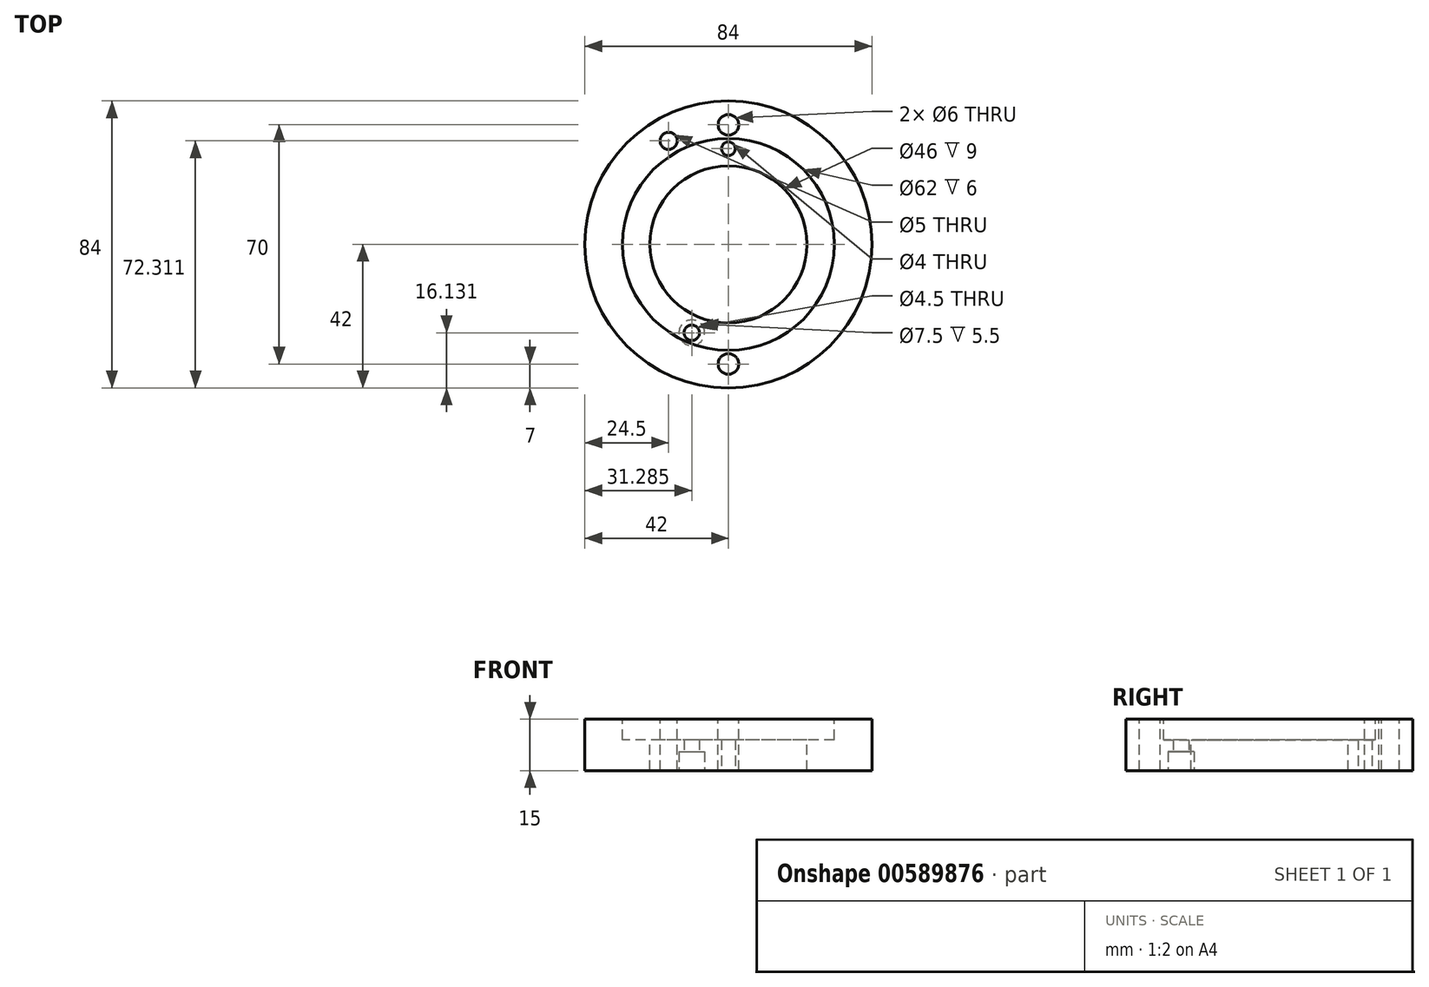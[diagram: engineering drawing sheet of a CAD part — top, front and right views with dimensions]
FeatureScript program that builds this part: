
annotation { "Feature Type Name" : "Feature", "Feature Type Description" : "" }
export const myFeature = defineFeature(function(context is Context, id is Id, definition is map)
    precondition{}
    {
        {
            var Q0;
            Q0=qCreatedBy(makeId("Top.planeOp"),FACE);
            var sketch = newSketch(context, id + "F0", { "sketchPlane" : qUnion([Q0])});
            skCircle(sketch, "E0", {"center": v(0, 0) * mm, "radius": 42 * mm});
            skCircle(sketch, "E1", {"center": v(0, 0) * mm, "radius": 23 * mm});
            skSolve(sketch);
        }
        {
            var Q0;
            Q0 = qSketchRegion(id + "F0", true);
            extrude(context, id + "F1", {"entities" : qUnion([Q0]), "oppositeDirection" : true, "depth" : 15 * mm, "offsetDistance" : 25 * mm});
        }
        {
            var Q0;
            Q0=makeQuery(id+"F1.opExtrude","CAP_FACE",FACE,{"disambiguationData":[OSD([sQuery(id+"F0.wireOp",EDGE,"E0"),sQuery(id+"F0.wireOp",EDGE,"E1")])],"isStart":true});
            var sketch = newSketch(context, id + "F2", { "sketchPlane" : qUnion([Q0])});
            skCircle(sketch, "E2", {"center": v(0, 0) * mm, "radius": 31 * mm});
            skSolve(sketch);
        }
        {
            var Q0;
            Q0=makeQuery(id+"F2.imprint","IMPRINT",FACE,{"disambiguationData":[TD([[makeQuery(id+"F2.imprint","IMPRINT",EDGE,{"derivedFrom":sQuery(id+"F2.wireOp",EDGE,"E2")}),1.0]])]});
            extrude(context, id + "F3", {"entities" : qUnion([Q0]), "operationType" : NewBodyOperationType.REMOVE, "oppositeDirection" : true, "depth" : 6 * mm, "offsetDistance" : 25 * mm});
        }
        {
            var Q0;
            Q0=makeQuery(id+"F1.opExtrude","CAP_FACE",FACE,{"disambiguationData":[OSD([sQuery(id+"F0.wireOp",EDGE,"E0"),sQuery(id+"F0.wireOp",EDGE,"E1")])],"isStart":true});
            var sketch = newSketch(context, id + "F4", { "sketchPlane" : qUnion([Q0])});
            skCircle(sketch, "E3", {"center": v(0, 35) * mm, "radius": 3 * mm});
            skCircle(sketch, "E4", {"center": v(0, -35) * mm, "radius": 3 * mm});
            skSolve(sketch);
        }
        {
            var Q0;
            Q0=makeQuery(id+"F4.imprint","IMPRINT",FACE,{"disambiguationData":[TD([[makeQuery(id+"F4.imprint","IMPRINT",EDGE,{"derivedFrom":sQuery(id+"F4.wireOp",EDGE,"E4")}),1.0]])]});
            var Q1;
            Q1=makeQuery(id+"F4.imprint","IMPRINT",FACE,{"disambiguationData":[TD([[makeQuery(id+"F4.imprint","IMPRINT",EDGE,{"derivedFrom":sQuery(id+"F4.wireOp",EDGE,"E3")}),1.0]])]});
            extrude(context, id + "F5", {"entities" : qUnion([Q0, Q1]), "operationType" : NewBodyOperationType.REMOVE, "endBound" : BoundingType.THROUGH_ALL, "oppositeDirection" : true, "depth" : 25 * mm, "offsetDistance" : 25 * mm});
        }
        {
            var Q0;
            Q0=makeQuery(id+"F1.opExtrude","CAP_FACE",FACE,{"disambiguationData":[OSD([sQuery(id+"F0.wireOp",EDGE,"E0"),sQuery(id+"F0.wireOp",EDGE,"E1")])],"isStart":true});
            var sketch = newSketch(context, id + "F6", { "sketchPlane" : qUnion([Q0])});
            skLineSegment(sketch, "E5", {"start": v(0, 0) * mm, "end": v(-21, 36.37) * mm, "construction": true});
            skCircle(sketch, "E6", {"center": v(0, 0) * mm, "radius": 35 * mm, "construction": true});
            skPoint(sketch, "E7", {"position": v(-17.5, 30.31) * mm});
            skSolve(sketch);
        }
        {
            var Q0;
            Q0=sQuery(id+"F6.wireOp",VERTEX,"E7");
            var Q1;
            Q1=makeQuery(id+"F1.opExtrude","SWEPT_BODY",BODY,{"disambiguationData":[OSD([sQuery(id+"F0.wireOp",EDGE,"E0"),sQuery(id+"F0.wireOp",EDGE,"E1")])]});
            hole(context, id + "F7", {"style" : HoleStyle.SIMPLE, "endStyle" : HoleEndStyle.THROUGH, "standardTappedOrClearance" : lookupTablePath({ "standard" : "ISO", "engagement" : "75%", "pitch" : "1 mm", "size" : "M6", "type" : "Tapped" }), "standardBlindInLast" : lookupTablePath({ "standard" : "ISO", "engagement" : "75%", "pitch" : "1 mm", "size" : "M6", "type" : "Tapped" }), "holeDiameter" : 5 * mm, "majorDiameter" : 6 * mm, "showTappedDepth" : true, "isTappedThrough" : true, "tappedDepth" : 12 * mm, "tapClearance" : 3, "locations" : qUnion([Q0]), "scope" : qUnion([Q1])});
        }
        {
            var Q0;
            Q0=makeQuery(id+"F1.opExtrude","CAP_FACE",FACE,{"disambiguationData":[OSD([sQuery(id+"F0.wireOp",EDGE,"E0"),sQuery(id+"F0.wireOp",EDGE,"E1")])],"isStart":false});
            var sketch = newSketch(context, id + "F8", { "sketchPlane" : qUnion([Q0])});
            skCircle(sketch, "E8", {"center": v(0, -28) * mm, "radius": 2 * mm});
            skSolve(sketch);
        }
        {
            var Q0;
            Q0=makeQuery(id+"F8.imprint","IMPRINT",FACE,{"disambiguationData":[TD([[makeQuery(id+"F8.imprint","IMPRINT",EDGE,{"derivedFrom":sQuery(id+"F8.wireOp",EDGE,"E8")}),1.0]])]});
            extrude(context, id + "F9", {"entities" : qUnion([Q0]), "operationType" : NewBodyOperationType.REMOVE, "endBound" : BoundingType.THROUGH_ALL, "oppositeDirection" : true, "depth" : 25 * mm, "offsetDistance" : 25 * mm});
        }
        {
            var Q0;
            Q0=makeQuery(id+"F1.opExtrude","CAP_FACE",FACE,{"disambiguationData":[OSD([sQuery(id+"F0.wireOp",EDGE,"E0"),sQuery(id+"F0.wireOp",EDGE,"E1")])],"isStart":false});
            var sketch = newSketch(context, id + "F10", { "sketchPlane" : qUnion([Q0])});
            skLineSegment(sketch, "E9", {"start": v(0, 0) * mm, "end": v(-12.25, 29.56) * mm, "construction": true});
            skCircle(sketch, "E10", {"center": v(0, 0) * mm, "radius": 28 * mm, "construction": true});
            skPoint(sketch, "E11", {"position": v(-10.72, 25.87) * mm});
            skSolve(sketch);
        }
        {
            var Q0;
            Q0=sQuery(id+"F10.wireOp",VERTEX,"E11");
            var Q1;
            Q1=makeQuery(id+"F1.opExtrude","SWEPT_BODY",BODY,{"disambiguationData":[OSD([sQuery(id+"F0.wireOp",EDGE,"E0"),sQuery(id+"F0.wireOp",EDGE,"E1")])]});
            hole(context, id + "F11", {"style" : HoleStyle.C_BORE, "endStyle" : HoleEndStyle.THROUGH, "holeDiameter" : 4.5 * mm, "cBoreDiameter" : 7.5 * mm, "cBoreDepth" : 5.5 * mm, "majorDiameter" : 6 * mm, "isTappedThrough" : true, "tappedDepth" : 12 * mm, "tapClearance" : 3, "locations" : qUnion([Q0]), "scope" : qUnion([Q1])});
        }
    });
